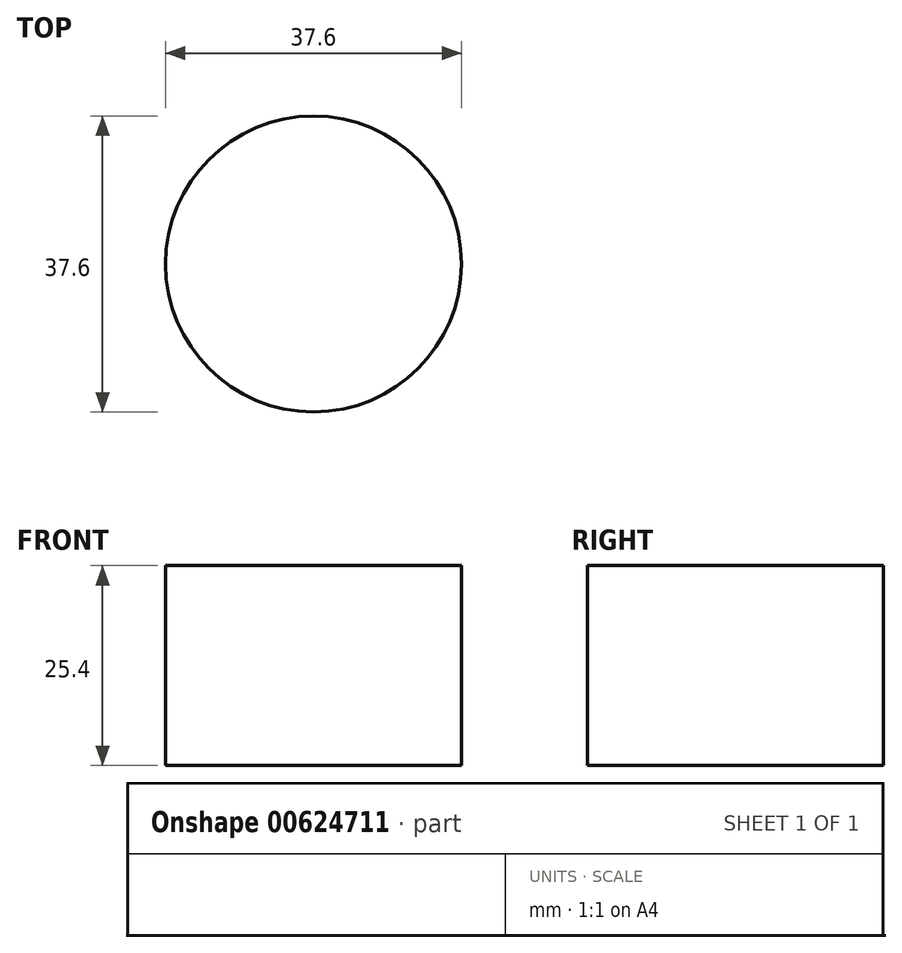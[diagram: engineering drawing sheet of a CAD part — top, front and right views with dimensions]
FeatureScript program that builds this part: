
annotation { "Feature Type Name" : "Feature", "Feature Type Description" : "" }
export const myFeature = defineFeature(function(context is Context, id is Id, definition is map)
    precondition{}
    {
        {
            var Q0;
            Q0=qCreatedBy(makeId("Top.planeOp"),FACE);
            var sketch = newSketch(context, id + "F0", { "sketchPlane" : qUnion([Q0])});
            skCircle(sketch, "E0", {"center": v(0, 0) * mm, "radius": 18.8 * mm});
            skSolve(sketch);
        }
        {
            var Q0;
            Q0 = qSketchRegion(id + "F0", true);
            extrude(context, id + "F1", {"entities" : qUnion([Q0]), "depth" : 25.4 * mm, "offsetDistance" : 25.4 * mm});
        }
    });
